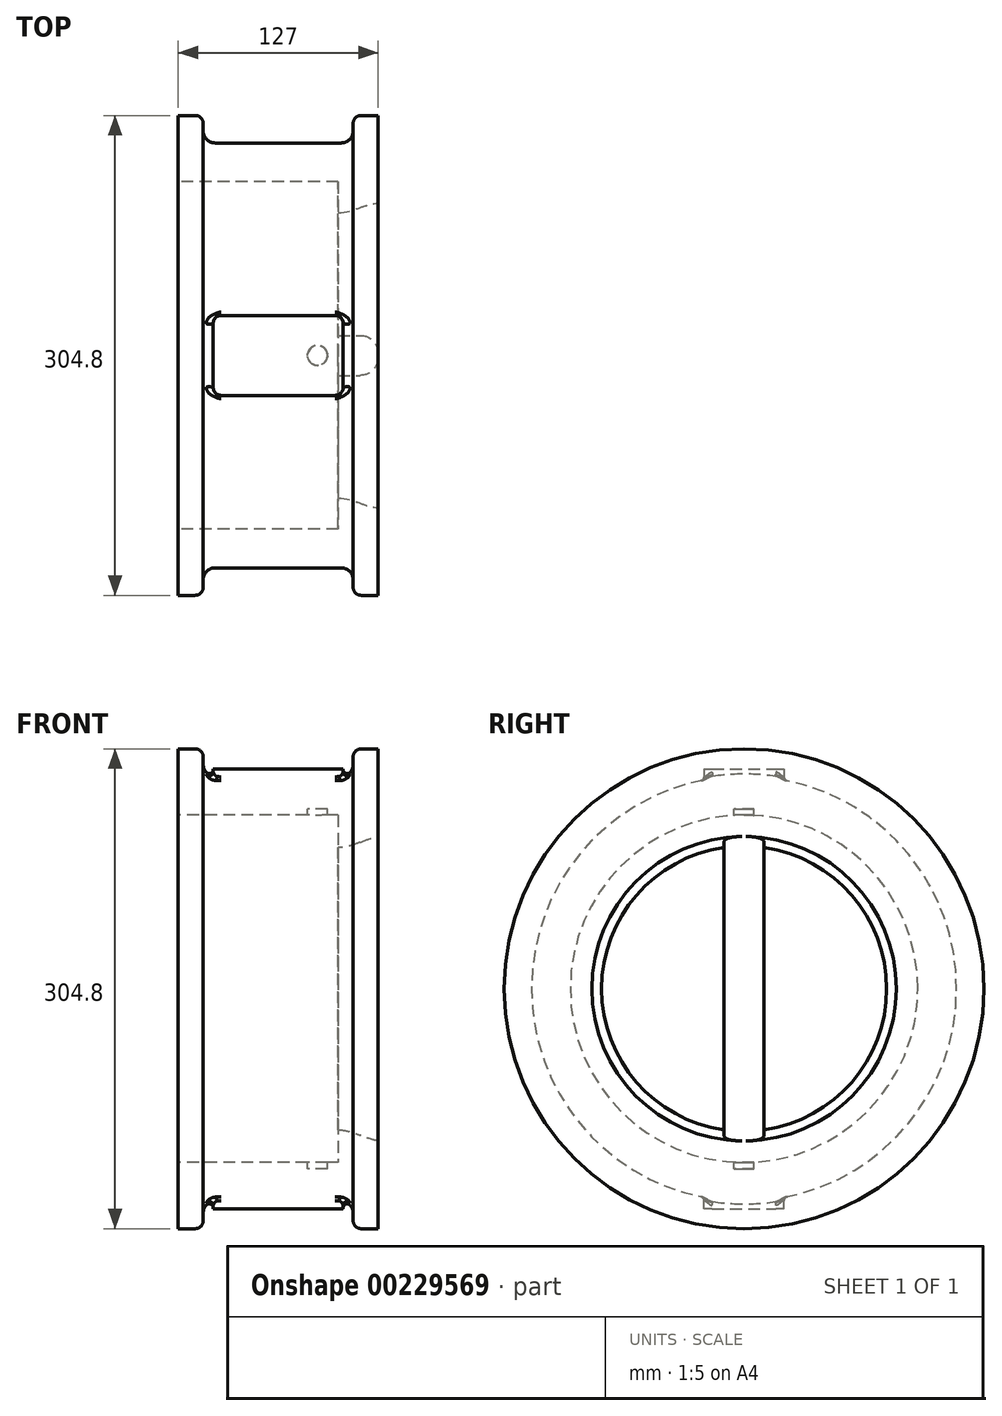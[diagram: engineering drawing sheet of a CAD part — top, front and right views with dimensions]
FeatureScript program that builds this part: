
annotation { "Feature Type Name" : "Feature", "Feature Type Description" : "" }
export const myFeature = defineFeature(function(context is Context, id is Id, definition is map)
    precondition{}
    {
        {
            var Q0;
            Q0=qCreatedBy(makeId("Front.planeOp"),FACE);
            var sketch = newSketch(context, id + "F0", { "sketchPlane" : qUnion([Q0])});
            skLineSegment(sketch, "E0", {"start": v(0, 0) * mm, "end": v(0, 110.36) * mm});
            skLineSegment(sketch, "E1", {"start": v(0, 0) * mm, "end": v(0, 152.4) * mm});
            skLineSegment(sketch, "E2", {"start": v(0, 152.4) * mm, "end": v(15.88, 152.4) * mm});
            skLineSegment(sketch, "E3", {"start": v(127, 152.4) * mm, "end": v(127, 110.36) * mm});
            skLineSegment(sketch, "E4", {"start": v(101.6, 110.36) * mm, "end": v(0, 110.36) * mm});
            skLineSegment(sketch, "E5.top", {"start": v(111.13, 134.94) * mm, "end": v(15.88, 134.94) * mm});
            skLineSegment(sketch, "E5.left", {"start": v(111.13, 152.4) * mm, "end": v(111.13, 134.94) * mm});
            skLineSegment(sketch, "E5.right", {"start": v(15.88, 152.4) * mm, "end": v(15.88, 134.94) * mm});
            skPoint(sketch, "E5.middle", {"position": v(63.5, 152.4) * mm});
            skLineSegment(sketch, "E6.trimOffspring", {"start": v(111.13, 152.4) * mm, "end": v(127, 152.4) * mm});
            skPoint(sketch, "E5.bottom.start.orphan", {"position": v(111.13, 169.86) * mm});
            skPoint(sketch, "E7.orphan", {"position": v(15.88, 169.86) * mm});
            skLineSegment(sketch, "E8", {"start": v(101.6, 90.55) * mm, "end": v(101.6, 110.36) * mm});
            skLineSegment(sketch, "E9", {"start": v(127, 110.36) * mm, "end": v(127, 96.71) * mm});
            skFitSpline(sketch, "E10", {"points": [v(101.6, 90.55) * mm, v(127, 96.71) * mm], "startDerivative": vector(27.9, 0) * mm, "endDerivative": vector(25.44, 0.85) * mm});
            skPoint(sketch, "E11.start.orphan", {"position": v(127, 0) * mm});
            skLineSegment(sketch, "E12", {"start": v(0, 0) * mm, "end": v(108.55, 0) * mm});
            skSolve(sketch);
        }
        {
            var Q0;
            Q0 = qSketchRegion(id + "F0", true);
            var Q1;
            Q1=sQuery(id+"F0.wireOp",EDGE,"E12");
            revolve(context, id + "F1", {"entities" : qUnion([Q0]), "axis" : qUnion([Q1]), "revolveType" : RevolveType.FULL});
        }
        {
            var Q0;
            Q0=makeQuery(id+"F1.opRevolve","SWEPT_EDGE",EDGE,{"disambiguationData":[OSD([sQuery(id+"F0.wireOp",EDGE,"E5.left"),sQuery(id+"F0.wireOp",EDGE,"E6.trimOffspring")])]});
            var Q1;
            Q1=makeQuery(id+"F1.opRevolve","SWEPT_EDGE",EDGE,{"disambiguationData":[OSD([sQuery(id+"F0.wireOp",EDGE,"E2"),sQuery(id+"F0.wireOp",EDGE,"E5.right")])]});
            fillet(context, id + "F2", {"entities" : qUnion([Q0, Q1]), "radius" : 5.08 * mm, "tangentPropagation" : true, "allowEdgeOverflow" : false});
        }
        {
            var Q0;
            Q0=makeQuery(id+"F1.opRevolve","SWEPT_EDGE",EDGE,{"disambiguationData":[OSD([sQuery(id+"F0.wireOp",EDGE,"E5.top"),sQuery(id+"F0.wireOp",EDGE,"E5.left")])]});
            var Q1;
            Q1=makeQuery(id+"F1.opRevolve","SWEPT_EDGE",EDGE,{"disambiguationData":[OSD([sQuery(id+"F0.wireOp",EDGE,"E5.top"),sQuery(id+"F0.wireOp",EDGE,"E5.right")])]});
            fillet(context, id + "F3", {"entities" : qUnion([Q0, Q1]), "radius" : 7.62 * mm, "tangentPropagation" : true, "allowEdgeOverflow" : false});
        }
        {
            var Q0;
            Q0=makeQuery(id+"F1.opRevolve","SWEPT_FACE",FACE,{"disambiguationData":[OSD([sQuery(id+"F0.wireOp",EDGE,"E8")])]});
            var sketch = newSketch(context, id + "F4", { "sketchPlane" : qUnion([Q0])});
            skLineSegment(sketch, "E13.bottom", {"start": v(12.7, 104.18) * mm, "end": v(-12.7, 104.18) * mm});
            skLineSegment(sketch, "E13.top", {"start": v(12.7, -104.18) * mm, "end": v(-12.7, -104.18) * mm});
            skLineSegment(sketch, "E13.left", {"start": v(12.7, 104.18) * mm, "end": v(12.7, -104.18) * mm});
            skLineSegment(sketch, "E13.right", {"start": v(-12.7, 104.18) * mm, "end": v(-12.7, -104.18) * mm});
            skPoint(sketch, "E13.middle", {"position": v(0, 0) * mm});
            skSolve(sketch);
        }
        {
            var Q0;
            Q0 = qSketchRegion(id + "F4", true);
            extrude(context, id + "F5", {"entities" : qUnion([Q0]), "operationType" : NewBodyOperationType.ADD, "oppositeDirection" : true, "depth" : 25.4 * mm});
        }
        {
            var Q0;
            Q0=makeQuery(id+"F5.opExtrude","CAP_EDGE",EDGE,{"disambiguationData":[OSD([sQuery(id+"F4.wireOp",EDGE,"E13.left")])],"isStart":false});
            var Q1;
            Q1=makeQuery(id+"F5.opExtrude","CAP_EDGE",EDGE,{"disambiguationData":[OSD([sQuery(id+"F4.wireOp",EDGE,"E13.right")])],"isStart":false});
            fillet(context, id + "F6", {"entities" : qUnion([Q0, Q1]), "radius" : 11.43 * mm, "tangentPropagation" : true, "allowEdgeOverflow" : false});
        }
        {
            var Q0;
            Q0=qCreatedBy(makeId("Top.planeOp"),FACE);
            cPlane(context, id + "F7", {"entities" : qUnion([Q0]), "cplaneType" : CPlaneType.OFFSET, "offset" : 114.3 * mm, "width" : 152.4 * mm, "height" : 152.4 * mm});
        }
        {
            var Q0;
            Q0=qCreatedBy(makeId("Top.planeOp"),FACE);
            cPlane(context, id + "F8", {"entities" : qUnion([Q0]), "cplaneType" : CPlaneType.OFFSET, "offset" : 114.3 * mm, "oppositeDirection" : true, "width" : 152.4 * mm, "height" : 152.4 * mm});
        }
        {
            var Q0;
            Q0=qCreatedBy(id+"F7.planeOp",FACE);
            var sketch = newSketch(context, id + "F9", { "sketchPlane" : qUnion([Q0])});
            skLineSegment(sketch, "E14.bottom", {"start": v(104.77, -25.4) * mm, "end": v(22.22, -25.4) * mm});
            skLineSegment(sketch, "E14.top", {"start": v(104.77, 25.4) * mm, "end": v(22.22, 25.4) * mm});
            skLineSegment(sketch, "E14.left", {"start": v(104.77, -25.4) * mm, "end": v(104.77, 25.4) * mm});
            skLineSegment(sketch, "E14.right", {"start": v(22.22, -25.4) * mm, "end": v(22.22, 25.4) * mm});
            skPoint(sketch, "E14.middle", {"position": v(63.5, 0) * mm});
            skLineSegment(sketch, "E15", {"start": v(23.78, 0) * mm, "end": v(110.07, 0) * mm});
            skPoint(sketch, "E15.endSnap0", {"position": v(104.77, 0) * mm});
            skLineSegment(sketch, "E16", {"start": v(63.5, 0) * mm, "end": v(63.5, 32.47) * mm});
            skSolve(sketch);
        }
        {
            var Q0;
            Q0 = qSketchRegion(id + "F9", true);
            extrude(context, id + "F10", {"entities" : qUnion([Q0]), "operationType" : NewBodyOperationType.ADD, "depth" : 25.4 * mm});
        }
        {
            var Q0;
            Q0=makeQuery(id+"F10.opExtrude","SWEPT_EDGE",EDGE,{"disambiguationData":[OSD([sQuery(id+"F9.wireOp",EDGE,"E14.top"),sQuery(id+"F9.wireOp",EDGE,"E14.left")])]});
            var Q1;
            Q1=makeQuery(id+"F10.opExtrude","SWEPT_EDGE",EDGE,{"disambiguationData":[OSD([sQuery(id+"F9.wireOp",EDGE,"E14.top"),sQuery(id+"F9.wireOp",EDGE,"E14.right")])]});
            var Q2;
            Q2=makeQuery(id+"F10.opExtrude","SWEPT_EDGE",EDGE,{"disambiguationData":[OSD([sQuery(id+"F9.wireOp",EDGE,"E14.bottom"),sQuery(id+"F9.wireOp",EDGE,"E14.right")])]});
            var Q3;
            Q3=makeQuery(id+"F10.opExtrude","SWEPT_EDGE",EDGE,{"disambiguationData":[OSD([sQuery(id+"F9.wireOp",EDGE,"E14.bottom"),sQuery(id+"F9.wireOp",EDGE,"E14.left")])]});
            fillet(context, id + "F11", {"entities" : qUnion([Q0, Q1, Q2, Q3]), "radius" : 5.08 * mm, "tangentPropagation" : true, "allowEdgeOverflow" : false});
        }
        {
            var Q0;
            Q0=makeQuery(id+"F10.boolean.opBoolean","INTERSECT",EDGE,{"derivedFrom":[makeQuery(id+"F1.opRevolve","SWEPT_FACE",FACE,{"disambiguationData":[OSD([sQuery(id+"F0.wireOp",EDGE,"E5.top")])]}),makeQuery(id+"F10.opExtrude","SWEPT_FACE",FACE,{"disambiguationData":[OSD([sQuery(id+"F9.wireOp",EDGE,"E14.bottom")])]})]});
            fillet(context, id + "F12", {"entities" : qUnion([Q0]), "radius" : 2.54 * mm, "tangentPropagation" : true, "allowEdgeOverflow" : false});
        }
        {
            var Q0;
            Q0=qCreatedBy(id+"F8.planeOp",FACE);
            var sketch = newSketch(context, id + "F13", { "sketchPlane" : qUnion([Q0])});
            skLineSegment(sketch, "E17", {"start": v(0, 0) * mm, "end": v(63.5, 0) * mm});
            skLineSegment(sketch, "E18.bottom", {"start": v(22.22, -25.4) * mm, "end": v(104.78, -25.4) * mm});
            skLineSegment(sketch, "E18.top", {"start": v(22.22, 25.4) * mm, "end": v(104.78, 25.4) * mm});
            skLineSegment(sketch, "E18.left", {"start": v(22.22, -25.4) * mm, "end": v(22.22, 25.4) * mm});
            skLineSegment(sketch, "E18.right", {"start": v(104.78, -25.4) * mm, "end": v(104.78, 25.4) * mm});
            skPoint(sketch, "E18.middle", {"position": v(63.5, 0) * mm});
            skSolve(sketch);
        }
        {
            var Q0;
            Q0 = qSketchRegion(id + "F13", true);
            extrude(context, id + "F14", {"entities" : qUnion([Q0]), "operationType" : NewBodyOperationType.ADD, "oppositeDirection" : true, "depth" : 25.4 * mm});
        }
        {
            var Q0;
            Q0=makeQuery(id+"F14.opExtrude","SWEPT_EDGE",EDGE,{"disambiguationData":[OSD([sQuery(id+"F13.wireOp",EDGE,"E18.top"),sQuery(id+"F13.wireOp",EDGE,"E18.left")])]});
            var Q1;
            Q1=makeQuery(id+"F14.opExtrude","SWEPT_EDGE",EDGE,{"disambiguationData":[OSD([sQuery(id+"F13.wireOp",EDGE,"E18.top"),sQuery(id+"F13.wireOp",EDGE,"E18.right")])]});
            var Q2;
            Q2=makeQuery(id+"F14.opExtrude","SWEPT_EDGE",EDGE,{"disambiguationData":[OSD([sQuery(id+"F13.wireOp",EDGE,"E18.bottom"),sQuery(id+"F13.wireOp",EDGE,"E18.right")])]});
            var Q3;
            Q3=makeQuery(id+"F14.opExtrude","SWEPT_EDGE",EDGE,{"disambiguationData":[OSD([sQuery(id+"F13.wireOp",EDGE,"E18.bottom"),sQuery(id+"F13.wireOp",EDGE,"E18.left")])]});
            fillet(context, id + "F15", {"entities" : qUnion([Q0, Q1, Q2, Q3]), "radius" : 5.08 * mm, "tangentPropagation" : true, "allowEdgeOverflow" : false});
        }
        {
            var Q0;
            Q0=makeQuery(id+"F14.boolean.opBoolean","INTERSECT",EDGE,{"derivedFrom":[makeQuery(id+"F1.opRevolve","SWEPT_FACE",FACE,{"disambiguationData":[OSD([sQuery(id+"F0.wireOp",EDGE,"E5.top")])]}),makeQuery(id+"F14.opExtrude","SWEPT_FACE",FACE,{"disambiguationData":[OSD([sQuery(id+"F13.wireOp",EDGE,"E18.bottom")])]})]});
            fillet(context, id + "F16", {"entities" : qUnion([Q0]), "radius" : 2.54 * mm, "tangentPropagation" : true, "allowEdgeOverflow" : false});
        }
        {
            var Q0;
            Q0=qCreatedBy(id+"F7.planeOp",FACE);
            var sketch = newSketch(context, id + "F17", { "sketchPlane" : qUnion([Q0])});
            skCircle(sketch, "E19", {"center": v(88.5, 0) * mm, "radius": 6.35 * mm});
            skSolve(sketch);
        }
        {
            var Q0;
            Q0 = qSketchRegion(id + "F17", true);
            extrude(context, id + "F18", {"entities" : qUnion([Q0]), "operationType" : NewBodyOperationType.REMOVE, "oppositeDirection" : true, "depth" : 228.6 * mm});
        }
    });
